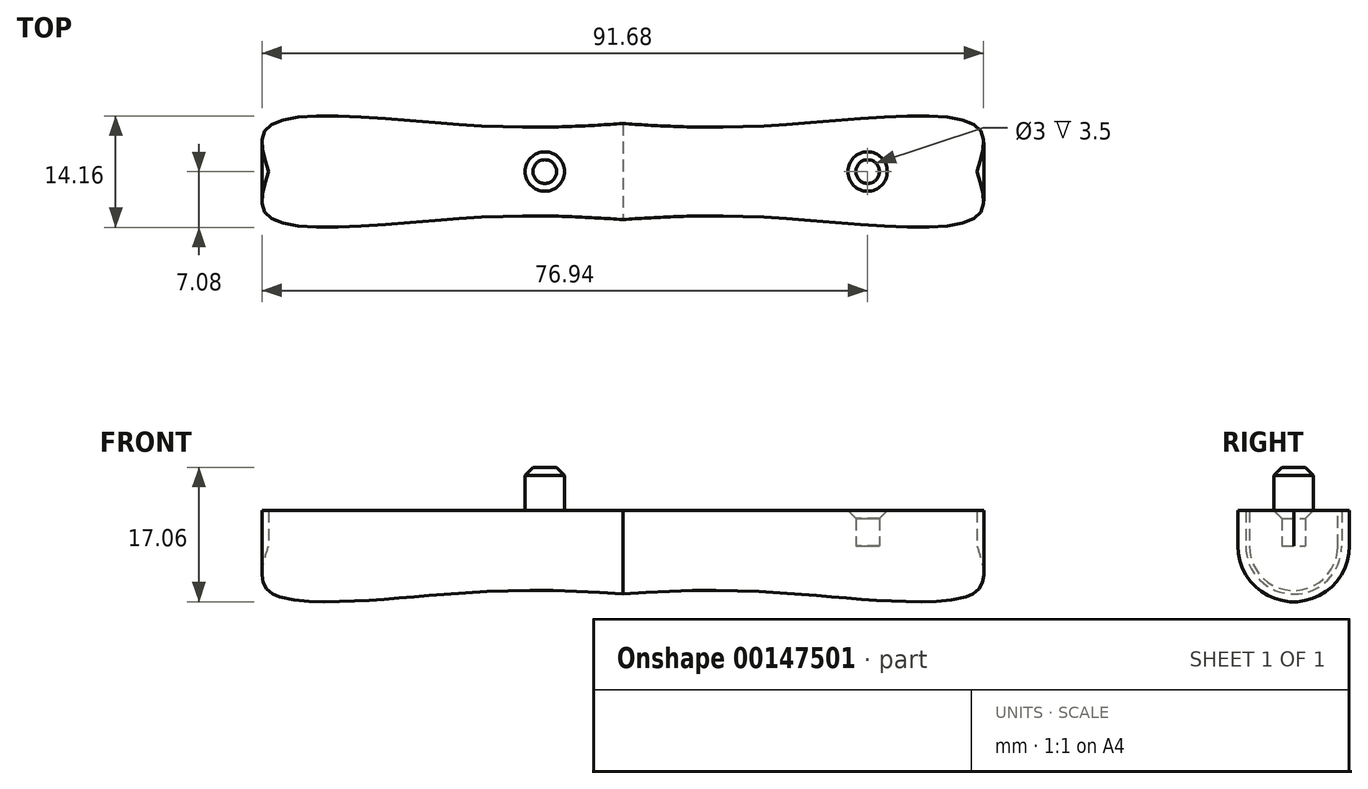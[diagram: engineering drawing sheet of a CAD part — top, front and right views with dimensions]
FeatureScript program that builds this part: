
annotation { "Feature Type Name" : "Feature", "Feature Type Description" : "" }
export const myFeature = defineFeature(function(context is Context, id is Id, definition is map)
    precondition{}
    {
        {
            var Q0;
            Q0=qCreatedBy(makeId("Top.planeOp"),FACE);
            var sketch = newSketch(context, id + "F0", { "sketchPlane" : qUnion([Q0])});
            skLineSegment(sketch, "E0", {"start": v(0, 0) * mm, "end": v(45, 0) * mm, "construction": true});
            skLineSegment(sketch, "E1", {"start": v(0, 0) * mm, "end": v(0, -6.1) * mm, "construction": true});
            skLineSegment(sketch, "E2.MirrorCS", {"start": v(0, 0) * mm, "end": v(-45, 0) * mm, "construction": true});
            skLineSegment(sketch, "E3.MirrorCS", {"start": v(0, 0) * mm, "end": v(0, 6.1) * mm, "construction": true});
            skPoint(sketch, "E4", {"position": v(-15, 5.9) * mm});
            skPoint(sketch, "E5", {"position": v(-25, 5.5) * mm});
            skPoint(sketch, "E6", {"position": v(-35, 4.5) * mm});
            skFitSpline(sketch, "E7", {"points": [v(-45, 0) * mm, v(0, 6.1) * mm], "startDerivative": vector(0, 17.1) * mm, "endDerivative": vector(58.73, 0.6) * mm});
            skFitSpline(sketch, "E8.MirrorCS", {"points": [v(45, 0) * mm, v(0, 6.1) * mm], "startDerivative": vector(0, 17.1) * mm, "endDerivative": vector(-58.73, 0.6) * mm});
            skFitSpline(sketch, "E9.MirrorCS", {"points": [v(-45, 0) * mm, v(0, -6.1) * mm], "startDerivative": vector(0, -17.1) * mm, "endDerivative": vector(58.73, -0.6) * mm});
            skFitSpline(sketch, "E10.MirrorCS", {"points": [v(45, 0) * mm, v(0, -6.1) * mm], "startDerivative": vector(0, -17.1) * mm, "endDerivative": vector(-58.73, -0.6) * mm});
            skSolve(sketch);
        }
        {
            var Q0;
            Q0=qCreatedBy(makeId("Top.planeOp"),FACE);
            var sketch = newSketch(context, id + "F1", { "sketchPlane" : qUnion([Q0])});
            skFitSpline(sketch, "E11.0", {"points": [v(-45, 0) * mm, v(-45, -5.7) * mm, v(-19.58, -5.9) * mm, v(0, -6.1) * mm]});
            skFitSpline(sketch, "E12.0", {"points": [v(45, 0) * mm, v(45, -5.7) * mm, v(19.58, -5.9) * mm, v(0, -6.1) * mm]});
            skLineSegment(sketch, "E13", {"start": v(-45, 0) * mm, "end": v(45, 0) * mm});
            skPoint(sketch, "E14.0.start.orphan", {"position": v(45, 0) * mm});
            skSolve(sketch);
        }
        {
            var Q0;
            Q0=makeQuery(id+"F1.imprint","IMPRINT",FACE,{"disambiguationData":[TD([[makeQuery(id+"F1.imprint","IMPRINT",EDGE,{"derivedFrom":sQuery(id+"F1.wireOp",EDGE,"E11.0")}),1.0]])]});
            var Q1;
            Q1=sQuery(id+"F1.wireOp",EDGE,"E11.0");
            var Q2;
            Q2=sQuery(id+"F1.wireOp",EDGE,"E12.0");
            var Q3;
            Q3=sQuery(id+"F1.wireOp",EDGE,"E13");
            revolve(context, id + "F2", {"surfaceOperationType" : NewSurfaceOperationType.NEW, "entities" : qUnion([Q0]), "surfaceEntities" : qUnion([Q1, Q2]), "axis" : qUnion([Q3]), "revolveType" : RevolveType.ONE_DIRECTION, "angle" : 180 * degree});
        }
        {
            var Q0;
            Q0=makeQuery(id+"F2.opRevolve","CAP_FACE",FACE,{"disambiguationData":[OSD([sQuery(id+"F1.wireOp",EDGE,"E11.0"),sQuery(id+"F1.wireOp",EDGE,"E12.0"),sQuery(id+"F1.wireOp",EDGE,"E13")])],"isStart":false});
            var sketch = newSketch(context, id + "F3", { "sketchPlane" : qUnion([Q0])});
            skCircle(sketch, "E15", {"center": v(-9.9, 0) * mm, "radius": 2.5 * mm});
            skLineSegment(sketch, "E16", {"start": v(-45, 0) * mm, "end": v(-45, -10.53) * mm, "construction": true});
            skCircle(sketch, "E17", {"center": v(-30.5, 0) * mm, "radius": 1.5 * mm});
            skLineSegment(sketch, "E18", {"start": v(0, 6.1) * mm, "end": v(0, -6.1) * mm, "construction": true});
            skCircle(sketch, "E19.MirrorC", {"center": v(31.1, 0) * mm, "radius": 1.5 * mm});
            skSolve(sketch);
        }
        {
            var Q0;
            Q0=makeQuery(id+"F3.imprint","IMPRINT",FACE,{"disambiguationData":[TD([[makeQuery(id+"F3.imprint","IMPRINT",EDGE,{"derivedFrom":sQuery(id+"F3.wireOp",EDGE,"E17")}),1.0]])]});
            var Q1;
            Q1=makeQuery(id+"F3.imprint","IMPRINT",FACE,{"disambiguationData":[TD([[makeQuery(id+"F3.imprint","IMPRINT",EDGE,{"derivedFrom":sQuery(id+"F3.wireOp",EDGE,"E19.MirrorC")}),-1.0]])]});
            extrude(context, id + "F4", {"entities" : qUnion([Q0, Q1]), "operationType" : NewBodyOperationType.ADD, "depth" : 4.5 * mm, "offsetDistance" : 25 * mm});
        }
        {
            var Q0;
            Q0=makeQuery(id+"F3.imprint","IMPRINT",FACE,{"disambiguationData":[TD([[makeQuery(id+"F3.imprint","IMPRINT",EDGE,{"derivedFrom":sQuery(id+"F3.wireOp",EDGE,"E15")}),1.0]])]});
            var Q1;
            Q1=sQuery(id+"F3.wireOp",EDGE,"E15");
            extrude(context, id + "F5", {"entities" : qUnion([Q0]), "operationType" : NewBodyOperationType.ADD, "surfaceEntities" : qUnion([Q1]), "depth" : 10 * mm, "offsetDistance" : 25 * mm});
        }
        {
            var Q0;
            Q0=makeQuery(id+"F4.opExtrude","CAP_EDGE",EDGE,{"disambiguationData":[OSD([sQuery(id+"F3.wireOp",EDGE,"E17")])],"isStart":false});
            var Q1;
            Q1=makeQuery(id+"F5.opExtrude","CAP_EDGE",EDGE,{"disambiguationData":[OSD([sQuery(id+"F3.wireOp",EDGE,"E15")])],"isStart":false});
            var Q2;
            Q2=makeQuery(id+"F4.opExtrude","CAP_EDGE",EDGE,{"disambiguationData":[OSD([sQuery(id+"F3.wireOp",EDGE,"E19.MirrorC")])],"isStart":false});
            chamfer(context, id + "F6", {"entities" : qUnion([Q0, Q1, Q2]), "width" : 1 * mm, "tangentPropagation" : true});
        }
    });
